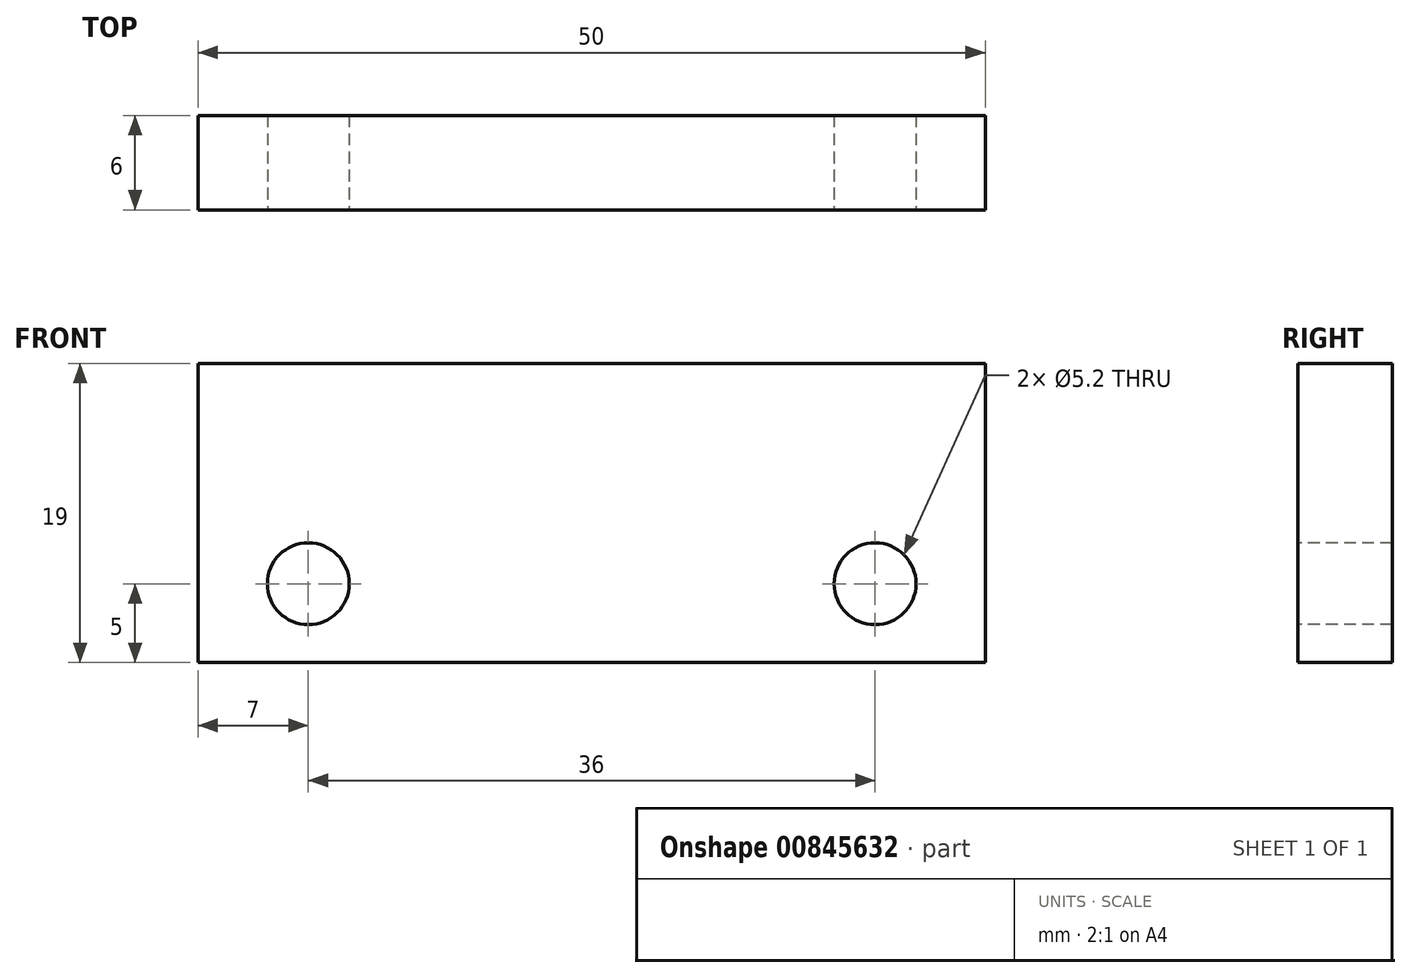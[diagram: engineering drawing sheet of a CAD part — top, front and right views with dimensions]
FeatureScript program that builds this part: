
annotation { "Feature Type Name" : "Feature", "Feature Type Description" : "" }
export const myFeature = defineFeature(function(context is Context, id is Id, definition is map)
    precondition{}
    {
        {
            var Q0;
            Q0=qCreatedBy(makeId("Front.planeOp"),FACE);
            var sketch = newSketch(context, id + "F0", { "sketchPlane" : qUnion([Q0])});
            skLineSegment(sketch, "E0.bottom", {"start": v(-25, 0) * mm, "end": v(25, 0) * mm});
            skLineSegment(sketch, "E0.top", {"start": v(-25, 19) * mm, "end": v(25, 19) * mm});
            skLineSegment(sketch, "E0.left", {"start": v(-25, 0) * mm, "end": v(-25, 19) * mm});
            skLineSegment(sketch, "E0.right", {"start": v(25, 0) * mm, "end": v(25, 19) * mm});
            skPoint(sketch, "E0.middle", {"position": v(0, 9.5) * mm});
            skLineSegment(sketch, "E1", {"start": v(-18, 5) * mm, "end": v(18, 5) * mm, "construction": true});
            skSolve(sketch);
        }
        {
            var Q0;
            Q0=makeQuery(id+"F0.imprint","IMPRINT",FACE,{"disambiguationData":[TD([[makeQuery(id+"F0.imprint","IMPRINT",EDGE,{"derivedFrom":sQuery(id+"F0.wireOp",EDGE,"E0.bottom")}),1.0]])]});
            extrude(context, id + "F1", {"entities" : qUnion([Q0]), "oppositeDirection" : true, "depth" : 6 * mm, "offsetDistance" : 25 * mm});
        }
        {
            var Q0;
            Q0=sQuery(id+"F0.wireOp",VERTEX,"E1.start");
            var Q1;
            Q1=sQuery(id+"F0.wireOp",VERTEX,"E1.end");
            var Q2;
            Q2=makeQuery(id+"F1.opExtrude","SWEPT_BODY",BODY,{"disambiguationData":[OSD([sQuery(id+"F0.wireOp",EDGE,"E0.bottom"),sQuery(id+"F0.wireOp",EDGE,"E0.top"),sQuery(id+"F0.wireOp",EDGE,"E0.left"),sQuery(id+"F0.wireOp",EDGE,"E0.right")])]});
            hole(context, id + "F2", {"style" : HoleStyle.SIMPLE, "endStyle" : HoleEndStyle.THROUGH, "holeDiameter" : 5.2 * mm, "majorDiameter" : 6 * mm, "isTappedThrough" : true, "tappedDepth" : 3 * mm, "tapClearance" : 3, "startFromSketch" : true, "locations" : qUnion([Q0, Q1]), "scope" : qUnion([Q2])});
        }
    });
